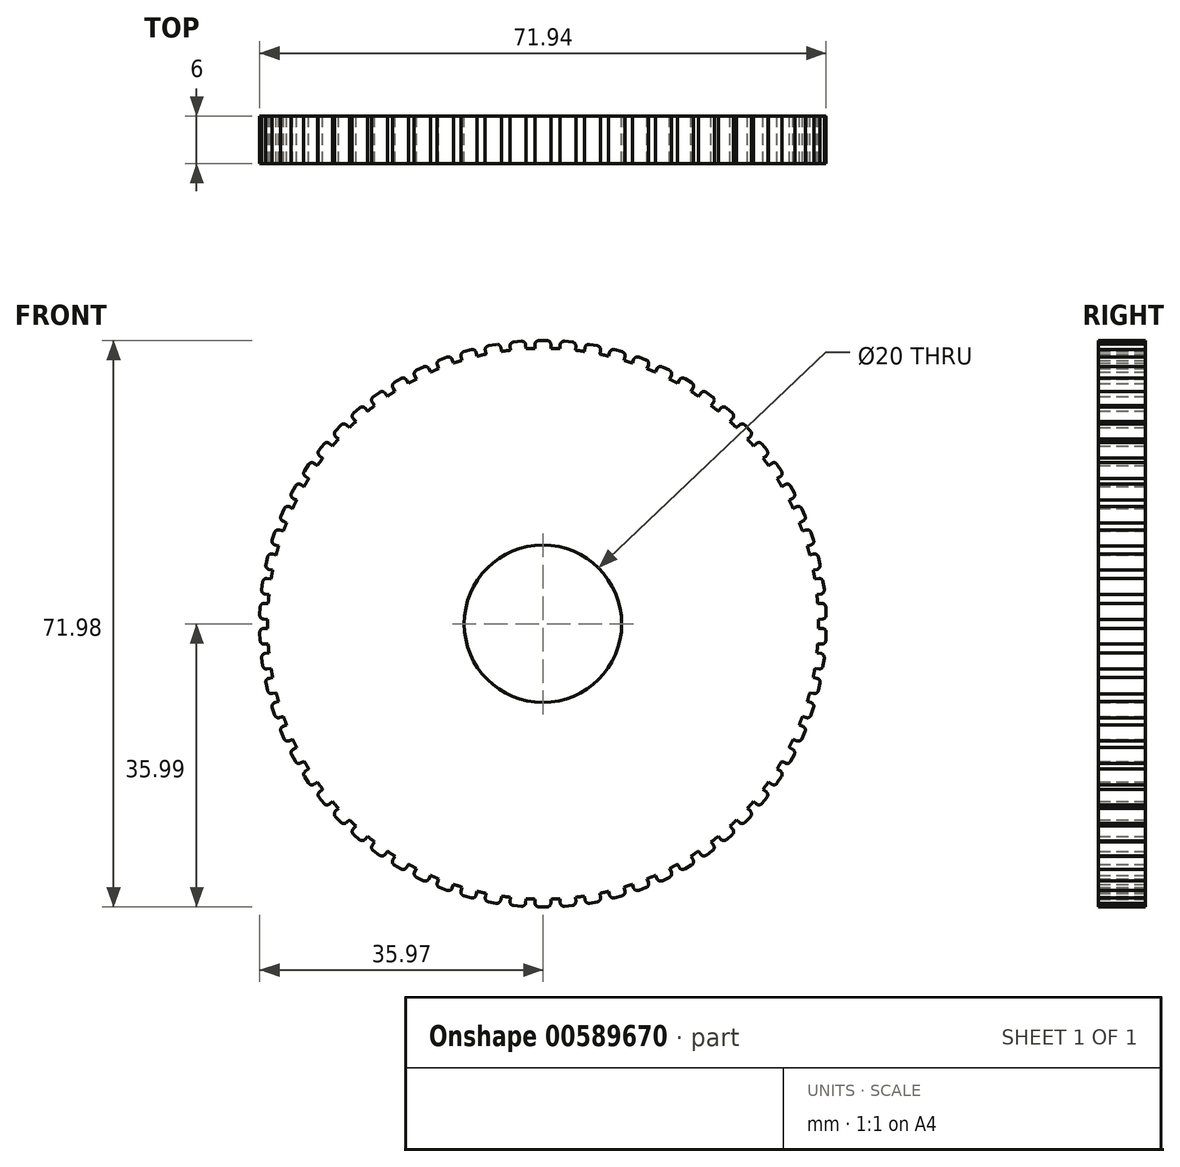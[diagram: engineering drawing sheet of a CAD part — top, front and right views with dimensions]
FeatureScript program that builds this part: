
annotation { "Feature Type Name" : "Feature", "Feature Type Description" : "" }
export const myFeature = defineFeature(function(context is Context, id is Id, definition is map)
    precondition{}
    {
        {
            var Q0;
            Q0=qCreatedBy(makeId("Front.planeOp"),FACE);
            var sketch = newSketch(context, id + "F0", { "sketchPlane" : qUnion([Q0])});
            skArc(sketch, "E0", {"start": v(-1, 34.99) * mm, "mid": v(-1.57, 34.96) * mm, "end": v(-2.14, 34.93) * mm});
            skLineSegment(sketch, "E1", {"start": v(-1, 34.99) * mm, "end": v(-1, 35.49) * mm});
            skLineSegment(sketch, "E2", {"start": v(-0.5, 35.99) * mm, "end": v(0.5, 35.99) * mm});
            skLineSegment(sketch, "E3", {"start": v(1, 35.49) * mm, "end": v(1, 34.99) * mm});
            skLineSegment(sketch, "E4", {"start": v(-2.15, 34.93) * mm, "end": v(-2.15, 35.96) * mm, "construction": true});
            skPoint(sketch, "E5.visualSharp", {"position": v(-1, 35.99) * mm});
            skArc(sketch, "E5.filletArc", {"start": v(-0.5, 35.99) * mm, "mid": v(-0.85, 35.84) * mm, "end": v(-1, 35.49) * mm});
            skPoint(sketch, "E6.visualSharp", {"position": v(1, 35.99) * mm});
            skArc(sketch, "E6.filletArc", {"start": v(1, 35.49) * mm, "mid": v(0.85, 35.84) * mm, "end": v(0.5, 35.99) * mm});
            skLineSegment(sketch, "E7.1.0", {"start": v(-4.13, 34.76) * mm, "end": v(-4.18, 35.25) * mm});
            skArc(sketch, "E7.1.1", {"start": v(-3.72, 35.8) * mm, "mid": v(-4.06, 35.62) * mm, "end": v(-4.18, 35.25) * mm});
            skLineSegment(sketch, "E7.1.2", {"start": v(-3.72, 35.8) * mm, "end": v(-2.73, 35.89) * mm});
            skArc(sketch, "E7.1.3", {"start": v(-2.18, 35.43) * mm, "mid": v(-2.36, 35.77) * mm, "end": v(-2.73, 35.89) * mm});
            skLineSegment(sketch, "E7.1.4", {"start": v(-2.18, 35.43) * mm, "end": v(-2.14, 34.93) * mm});
            skLineSegment(sketch, "E7.1.5", {"start": v(-5.27, 34.6) * mm, "end": v(-5.36, 35.62) * mm, "construction": true});
            skLineSegment(sketch, "E7.2.0", {"start": v(-7.23, 34.24) * mm, "end": v(-7.32, 34.74) * mm});
            skArc(sketch, "E7.2.1", {"start": v(-6.92, 35.32) * mm, "mid": v(-7.24, 35.11) * mm, "end": v(-7.32, 34.74) * mm});
            skLineSegment(sketch, "E7.2.2", {"start": v(-6.92, 35.32) * mm, "end": v(-5.93, 35.5) * mm});
            skArc(sketch, "E7.2.3", {"start": v(-5.35, 35.1) * mm, "mid": v(-5.56, 35.42) * mm, "end": v(-5.93, 35.5) * mm});
            skLineSegment(sketch, "E7.2.4", {"start": v(-5.35, 35.1) * mm, "end": v(-5.26, 34.6) * mm});
            skLineSegment(sketch, "E7.2.5", {"start": v(-8.35, 33.99) * mm, "end": v(-8.53, 35) * mm, "construction": true});
            skLineSegment(sketch, "E7.3.0", {"start": v(-10.27, 33.46) * mm, "end": v(-10.4, 33.94) * mm});
            skArc(sketch, "E7.3.1", {"start": v(-10.06, 34.56) * mm, "mid": v(-10.36, 34.32) * mm, "end": v(-10.4, 33.94) * mm});
            skLineSegment(sketch, "E7.3.2", {"start": v(-10.06, 34.56) * mm, "end": v(-9.1, 34.82) * mm});
            skArc(sketch, "E7.3.3", {"start": v(-8.48, 34.47) * mm, "mid": v(-8.71, 34.77) * mm, "end": v(-9.1, 34.82) * mm});
            skLineSegment(sketch, "E7.3.4", {"start": v(-8.48, 34.47) * mm, "end": v(-8.34, 34) * mm});
            skLineSegment(sketch, "E7.3.5", {"start": v(-11.36, 33.1) * mm, "end": v(-11.64, 34.1) * mm, "construction": true});
            skLineSegment(sketch, "E7.4.0", {"start": v(-13.23, 32.4) * mm, "end": v(-13.4, 32.87) * mm});
            skArc(sketch, "E7.4.1", {"start": v(-13.11, 33.52) * mm, "mid": v(-13.4, 33.25) * mm, "end": v(-13.4, 32.87) * mm});
            skLineSegment(sketch, "E7.4.2", {"start": v(-13.11, 33.52) * mm, "end": v(-12.18, 33.87) * mm});
            skArc(sketch, "E7.4.3", {"start": v(-11.53, 33.57) * mm, "mid": v(-11.8, 33.85) * mm, "end": v(-12.18, 33.87) * mm});
            skLineSegment(sketch, "E7.4.4", {"start": v(-11.53, 33.57) * mm, "end": v(-11.36, 33.1) * mm});
            skLineSegment(sketch, "E7.4.5", {"start": v(-14.28, 31.95) * mm, "end": v(-14.65, 32.91) * mm, "construction": true});
            skLineSegment(sketch, "E7.5.0", {"start": v(-16.08, 31.09) * mm, "end": v(-16.3, 31.54) * mm});
            skArc(sketch, "E7.5.1", {"start": v(-16.06, 32.2) * mm, "mid": v(-16.32, 31.92) * mm, "end": v(-16.3, 31.54) * mm});
            skLineSegment(sketch, "E7.5.2", {"start": v(-16.06, 32.2) * mm, "end": v(-15.16, 32.64) * mm});
            skArc(sketch, "E7.5.3", {"start": v(-14.5, 32.4) * mm, "mid": v(-14.78, 32.66) * mm, "end": v(-15.16, 32.64) * mm});
            skLineSegment(sketch, "E7.5.4", {"start": v(-14.5, 32.4) * mm, "end": v(-14.28, 31.95) * mm});
            skLineSegment(sketch, "E7.5.5", {"start": v(-17.1, 30.54) * mm, "end": v(-17.54, 31.47) * mm, "construction": true});
            skLineSegment(sketch, "E7.6.0", {"start": v(-18.8, 29.52) * mm, "end": v(-19.06, 29.95) * mm});
            skArc(sketch, "E7.6.1", {"start": v(-18.89, 30.64) * mm, "mid": v(-19.11, 30.33) * mm, "end": v(-19.06, 29.95) * mm});
            skLineSegment(sketch, "E7.6.2", {"start": v(-18.89, 30.64) * mm, "end": v(-18.03, 31.15) * mm});
            skArc(sketch, "E7.6.3", {"start": v(-17.34, 30.98) * mm, "mid": v(-17.65, 31.2) * mm, "end": v(-18.03, 31.15) * mm});
            skLineSegment(sketch, "E7.6.4", {"start": v(-17.34, 30.98) * mm, "end": v(-17.09, 30.55) * mm});
            skLineSegment(sketch, "E7.6.5", {"start": v(-19.76, 28.89) * mm, "end": v(-20.29, 29.77) * mm, "construction": true});
            skLineSegment(sketch, "E7.7.0", {"start": v(-21.37, 27.72) * mm, "end": v(-21.67, 28.12) * mm});
            skArc(sketch, "E7.7.1", {"start": v(-21.56, 28.82) * mm, "mid": v(-21.76, 28.5) * mm, "end": v(-21.67, 28.12) * mm});
            skLineSegment(sketch, "E7.7.2", {"start": v(-21.56, 28.82) * mm, "end": v(-20.75, 29.4) * mm});
            skArc(sketch, "E7.7.3", {"start": v(-20.05, 29.3) * mm, "mid": v(-20.38, 29.5) * mm, "end": v(-20.75, 29.4) * mm});
            skLineSegment(sketch, "E7.7.4", {"start": v(-20.05, 29.3) * mm, "end": v(-19.76, 28.9) * mm});
            skLineSegment(sketch, "E7.7.5", {"start": v(-22.27, 27) * mm, "end": v(-22.87, 27.83) * mm, "construction": true});
            skLineSegment(sketch, "E7.8.0", {"start": v(-23.77, 25.69) * mm, "end": v(-24.1, 26.07) * mm});
            skArc(sketch, "E7.8.1", {"start": v(-24.05, 26.77) * mm, "mid": v(-24.22, 26.43) * mm, "end": v(-24.1, 26.07) * mm});
            skLineSegment(sketch, "E7.8.2", {"start": v(-24.05, 26.77) * mm, "end": v(-23.3, 27.43) * mm});
            skArc(sketch, "E7.8.3", {"start": v(-22.6, 27.38) * mm, "mid": v(-22.94, 27.55) * mm, "end": v(-23.3, 27.43) * mm});
            skLineSegment(sketch, "E7.8.4", {"start": v(-22.6, 27.38) * mm, "end": v(-22.27, 27) * mm});
            skLineSegment(sketch, "E7.8.5", {"start": v(-24.6, 24.9) * mm, "end": v(-25.28, 25.67) * mm, "construction": true});
            skLineSegment(sketch, "E7.9.0", {"start": v(-25.98, 23.45) * mm, "end": v(-26.34, 23.8) * mm});
            skArc(sketch, "E7.9.1", {"start": v(-26.36, 24.5) * mm, "mid": v(-26.5, 24.15) * mm, "end": v(-26.34, 23.8) * mm});
            skLineSegment(sketch, "E7.9.2", {"start": v(-26.36, 24.5) * mm, "end": v(-25.66, 25.23) * mm});
            skArc(sketch, "E7.9.3", {"start": v(-24.96, 25.25) * mm, "mid": v(-25.31, 25.38) * mm, "end": v(-25.66, 25.23) * mm});
            skLineSegment(sketch, "E7.9.4", {"start": v(-24.96, 25.25) * mm, "end": v(-24.6, 24.9) * mm});
            skLineSegment(sketch, "E7.9.5", {"start": v(-26.73, 22.6) * mm, "end": v(-27.48, 23.3) * mm, "construction": true});
            skLineSegment(sketch, "E7.10.0", {"start": v(-27.98, 21.03) * mm, "end": v(-28.37, 21.34) * mm});
            skArc(sketch, "E7.10.1", {"start": v(-28.45, 22.05) * mm, "mid": v(-28.55, 21.68) * mm, "end": v(-28.37, 21.34) * mm});
            skLineSegment(sketch, "E7.10.2", {"start": v(-28.45, 22.05) * mm, "end": v(-27.82, 22.83) * mm});
            skArc(sketch, "E7.10.3", {"start": v(-27.12, 22.9) * mm, "mid": v(-27.49, 23.01) * mm, "end": v(-27.82, 22.83) * mm});
            skLineSegment(sketch, "E7.10.4", {"start": v(-27.12, 22.9) * mm, "end": v(-26.73, 22.6) * mm});
            skLineSegment(sketch, "E7.10.5", {"start": v(-28.65, 20.1) * mm, "end": v(-29.45, 20.74) * mm, "construction": true});
            skLineSegment(sketch, "E7.11.0", {"start": v(-29.75, 18.44) * mm, "end": v(-30.17, 18.71) * mm});
            skArc(sketch, "E7.11.1", {"start": v(-30.3, 19.4) * mm, "mid": v(-30.38, 19.03) * mm, "end": v(-30.17, 18.71) * mm});
            skLineSegment(sketch, "E7.11.2", {"start": v(-30.3, 19.4) * mm, "end": v(-29.76, 20.24) * mm});
            skArc(sketch, "E7.11.3", {"start": v(-29.06, 20.38) * mm, "mid": v(-29.44, 20.46) * mm, "end": v(-29.76, 20.24) * mm});
            skLineSegment(sketch, "E7.11.4", {"start": v(-29.06, 20.38) * mm, "end": v(-28.65, 20.1) * mm});
            skLineSegment(sketch, "E7.11.5", {"start": v(-30.34, 17.45) * mm, "end": v(-31.2, 18.02) * mm, "construction": true});
            skLineSegment(sketch, "E7.12.0", {"start": v(-31.28, 15.7) * mm, "end": v(-31.72, 15.93) * mm});
            skArc(sketch, "E7.12.1", {"start": v(-31.93, 16.61) * mm, "mid": v(-31.96, 16.23) * mm, "end": v(-31.72, 15.93) * mm});
            skLineSegment(sketch, "E7.12.2", {"start": v(-31.93, 16.61) * mm, "end": v(-31.45, 17.5) * mm});
            skArc(sketch, "E7.12.3", {"start": v(-30.77, 17.7) * mm, "mid": v(-31.16, 17.73) * mm, "end": v(-31.45, 17.5) * mm});
            skLineSegment(sketch, "E7.12.4", {"start": v(-30.77, 17.7) * mm, "end": v(-30.33, 17.46) * mm});
            skLineSegment(sketch, "E7.12.5", {"start": v(-31.78, 14.66) * mm, "end": v(-32.68, 15.15) * mm, "construction": true});
            skLineSegment(sketch, "E7.13.0", {"start": v(-32.56, 12.83) * mm, "end": v(-33.02, 13.03) * mm});
            skArc(sketch, "E7.13.1", {"start": v(-33.29, 13.68) * mm, "mid": v(-33.3, 13.3) * mm, "end": v(-33.02, 13.03) * mm});
            skLineSegment(sketch, "E7.13.2", {"start": v(-33.29, 13.68) * mm, "end": v(-32.9, 14.6) * mm});
            skArc(sketch, "E7.13.3", {"start": v(-32.24, 14.87) * mm, "mid": v(-32.62, 14.87) * mm, "end": v(-32.9, 14.6) * mm});
            skLineSegment(sketch, "E7.13.4", {"start": v(-32.24, 14.87) * mm, "end": v(-31.78, 14.67) * mm});
            skLineSegment(sketch, "E7.13.5", {"start": v(-32.97, 11.76) * mm, "end": v(-33.91, 12.16) * mm, "construction": true});
            skLineSegment(sketch, "E7.14.0", {"start": v(-33.58, 9.86) * mm, "end": v(-34.06, 10.01) * mm});
            skArc(sketch, "E7.14.1", {"start": v(-34.38, 10.64) * mm, "mid": v(-34.35, 10.26) * mm, "end": v(-34.06, 10.01) * mm});
            skLineSegment(sketch, "E7.14.2", {"start": v(-34.38, 10.64) * mm, "end": v(-34.07, 11.6) * mm});
            skArc(sketch, "E7.14.3", {"start": v(-33.44, 11.92) * mm, "mid": v(-33.82, 11.89) * mm, "end": v(-34.07, 11.6) * mm});
            skLineSegment(sketch, "E7.14.4", {"start": v(-33.44, 11.92) * mm, "end": v(-32.96, 11.76) * mm});
            skLineSegment(sketch, "E7.14.5", {"start": v(-33.89, 8.75) * mm, "end": v(-34.86, 9.07) * mm, "construction": true});
            skLineSegment(sketch, "E7.15.0", {"start": v(-34.33, 6.81) * mm, "end": v(-34.82, 6.92) * mm});
            skArc(sketch, "E7.15.1", {"start": v(-35.2, 7.52) * mm, "mid": v(-35.13, 7.14) * mm, "end": v(-34.82, 6.92) * mm});
            skLineSegment(sketch, "E7.15.2", {"start": v(-35.2, 7.52) * mm, "end": v(-34.97, 8.5) * mm});
            skArc(sketch, "E7.15.3", {"start": v(-34.37, 8.87) * mm, "mid": v(-34.75, 8.8) * mm, "end": v(-34.97, 8.5) * mm});
            skLineSegment(sketch, "E7.15.4", {"start": v(-34.37, 8.87) * mm, "end": v(-33.89, 8.76) * mm});
            skLineSegment(sketch, "E7.15.5", {"start": v(-34.54, 5.68) * mm, "end": v(-35.54, 5.91) * mm, "construction": true});
            skLineSegment(sketch, "E7.16.0", {"start": v(-34.8, 3.7) * mm, "end": v(-35.3, 3.77) * mm});
            skArc(sketch, "E7.16.1", {"start": v(-35.73, 4.34) * mm, "mid": v(-35.63, 3.96) * mm, "end": v(-35.3, 3.77) * mm});
            skLineSegment(sketch, "E7.16.2", {"start": v(-35.73, 4.34) * mm, "end": v(-35.6, 5.33) * mm});
            skArc(sketch, "E7.16.3", {"start": v(-35.03, 5.75) * mm, "mid": v(-35.4, 5.66) * mm, "end": v(-35.6, 5.33) * mm});
            skLineSegment(sketch, "E7.16.4", {"start": v(-35.03, 5.75) * mm, "end": v(-34.53, 5.69) * mm});
            skLineSegment(sketch, "E7.16.5", {"start": v(-34.9, 2.56) * mm, "end": v(-35.92, 2.7) * mm, "construction": true});
            skLineSegment(sketch, "E7.17.0", {"start": v(-35, 0.57) * mm, "end": v(-35.5, 0.6) * mm});
            skArc(sketch, "E7.17.1", {"start": v(-35.97, 1.11) * mm, "mid": v(-35.84, 0.76) * mm, "end": v(-35.5, 0.6) * mm});
            skLineSegment(sketch, "E7.17.2", {"start": v(-35.97, 1.11) * mm, "end": v(-35.93, 2.11) * mm});
            skArc(sketch, "E7.17.3", {"start": v(-35.4, 2.6) * mm, "mid": v(-35.76, 2.46) * mm, "end": v(-35.93, 2.11) * mm});
            skLineSegment(sketch, "E7.17.4", {"start": v(-35.4, 2.6) * mm, "end": v(-34.9, 2.57) * mm});
            skLineSegment(sketch, "E7.17.5", {"start": v(-35, -0.58) * mm, "end": v(-36.02, -0.53) * mm, "construction": true});
            skLineSegment(sketch, "E7.18.0", {"start": v(-34.9, -2.57) * mm, "end": v(-35.4, -2.6) * mm});
            skArc(sketch, "E7.18.1", {"start": v(-35.93, -2.11) * mm, "mid": v(-35.76, -2.46) * mm, "end": v(-35.4, -2.6) * mm});
            skLineSegment(sketch, "E7.18.2", {"start": v(-35.93, -2.11) * mm, "end": v(-35.97, -1.11) * mm});
            skArc(sketch, "E7.18.3", {"start": v(-35.5, -0.6) * mm, "mid": v(-35.84, -0.76) * mm, "end": v(-35.97, -1.11) * mm});
            skLineSegment(sketch, "E7.18.4", {"start": v(-35.5, -0.6) * mm, "end": v(-35, -0.57) * mm});
            skLineSegment(sketch, "E7.18.5", {"start": v(-34.8, -3.71) * mm, "end": v(-35.83, -3.76) * mm, "construction": true});
            skLineSegment(sketch, "E7.19.0", {"start": v(-34.53, -5.69) * mm, "end": v(-35.03, -5.75) * mm});
            skArc(sketch, "E7.19.1", {"start": v(-35.6, -5.33) * mm, "mid": v(-35.4, -5.66) * mm, "end": v(-35.03, -5.75) * mm});
            skLineSegment(sketch, "E7.19.2", {"start": v(-35.6, -5.33) * mm, "end": v(-35.73, -4.34) * mm});
            skArc(sketch, "E7.19.3", {"start": v(-35.3, -3.77) * mm, "mid": v(-35.63, -3.96) * mm, "end": v(-35.73, -4.34) * mm});
            skLineSegment(sketch, "E7.19.4", {"start": v(-35.3, -3.77) * mm, "end": v(-34.8, -3.7) * mm});
            skLineSegment(sketch, "E7.19.5", {"start": v(-34.33, -6.82) * mm, "end": v(-35.35, -6.95) * mm, "construction": true});
            skLineSegment(sketch, "E7.20.0", {"start": v(-33.89, -8.76) * mm, "end": v(-34.37, -8.87) * mm});
            skArc(sketch, "E7.20.1", {"start": v(-34.97, -8.5) * mm, "mid": v(-34.75, -8.8) * mm, "end": v(-34.37, -8.87) * mm});
            skLineSegment(sketch, "E7.20.2", {"start": v(-34.97, -8.5) * mm, "end": v(-35.2, -7.52) * mm});
            skArc(sketch, "E7.20.3", {"start": v(-34.82, -6.92) * mm, "mid": v(-35.13, -7.14) * mm, "end": v(-35.2, -7.52) * mm});
            skLineSegment(sketch, "E7.20.4", {"start": v(-34.82, -6.92) * mm, "end": v(-34.33, -6.81) * mm});
            skLineSegment(sketch, "E7.20.5", {"start": v(-33.58, -9.87) * mm, "end": v(-34.58, -10.1) * mm, "construction": true});
            skLineSegment(sketch, "E7.21.0", {"start": v(-32.96, -11.76) * mm, "end": v(-33.44, -11.92) * mm});
            skArc(sketch, "E7.21.1", {"start": v(-34.07, -11.6) * mm, "mid": v(-33.82, -11.89) * mm, "end": v(-33.44, -11.92) * mm});
            skLineSegment(sketch, "E7.21.2", {"start": v(-34.07, -11.6) * mm, "end": v(-34.38, -10.64) * mm});
            skArc(sketch, "E7.21.3", {"start": v(-34.06, -10.01) * mm, "mid": v(-34.35, -10.26) * mm, "end": v(-34.38, -10.64) * mm});
            skLineSegment(sketch, "E7.21.4", {"start": v(-34.06, -10.01) * mm, "end": v(-33.58, -9.86) * mm});
            skLineSegment(sketch, "E7.21.5", {"start": v(-32.56, -12.84) * mm, "end": v(-33.54, -13.15) * mm, "construction": true});
            skLineSegment(sketch, "E7.22.0", {"start": v(-31.78, -14.67) * mm, "end": v(-32.24, -14.87) * mm});
            skArc(sketch, "E7.22.1", {"start": v(-32.9, -14.6) * mm, "mid": v(-32.62, -14.87) * mm, "end": v(-32.24, -14.87) * mm});
            skLineSegment(sketch, "E7.22.2", {"start": v(-32.9, -14.6) * mm, "end": v(-33.29, -13.68) * mm});
            skArc(sketch, "E7.22.3", {"start": v(-33.02, -13.03) * mm, "mid": v(-33.3, -13.3) * mm, "end": v(-33.29, -13.68) * mm});
            skLineSegment(sketch, "E7.22.4", {"start": v(-33.02, -13.03) * mm, "end": v(-32.56, -12.83) * mm});
            skLineSegment(sketch, "E7.22.5", {"start": v(-31.28, -15.7) * mm, "end": v(-32.22, -16.1) * mm, "construction": true});
            skLineSegment(sketch, "E7.23.0", {"start": v(-30.33, -17.46) * mm, "end": v(-30.77, -17.7) * mm});
            skArc(sketch, "E7.23.1", {"start": v(-31.45, -17.5) * mm, "mid": v(-31.16, -17.73) * mm, "end": v(-30.77, -17.7) * mm});
            skLineSegment(sketch, "E7.23.2", {"start": v(-31.45, -17.5) * mm, "end": v(-31.93, -16.61) * mm});
            skArc(sketch, "E7.23.3", {"start": v(-31.72, -15.93) * mm, "mid": v(-31.96, -16.23) * mm, "end": v(-31.93, -16.61) * mm});
            skLineSegment(sketch, "E7.23.4", {"start": v(-31.72, -15.93) * mm, "end": v(-31.28, -15.7) * mm});
            skLineSegment(sketch, "E7.23.5", {"start": v(-29.75, -18.44) * mm, "end": v(-30.65, -18.93) * mm, "construction": true});
            skLineSegment(sketch, "E7.24.0", {"start": v(-28.65, -20.1) * mm, "end": v(-29.06, -20.38) * mm});
            skArc(sketch, "E7.24.1", {"start": v(-29.76, -20.24) * mm, "mid": v(-29.44, -20.46) * mm, "end": v(-29.06, -20.38) * mm});
            skLineSegment(sketch, "E7.24.2", {"start": v(-29.76, -20.24) * mm, "end": v(-30.3, -19.4) * mm});
            skArc(sketch, "E7.24.3", {"start": v(-30.17, -18.71) * mm, "mid": v(-30.38, -19.03) * mm, "end": v(-30.3, -19.4) * mm});
            skLineSegment(sketch, "E7.24.4", {"start": v(-30.17, -18.71) * mm, "end": v(-29.75, -18.44) * mm});
            skLineSegment(sketch, "E7.24.5", {"start": v(-27.97, -21.04) * mm, "end": v(-28.83, -21.6) * mm, "construction": true});
            skLineSegment(sketch, "E7.25.0", {"start": v(-26.73, -22.6) * mm, "end": v(-27.12, -22.9) * mm});
            skArc(sketch, "E7.25.1", {"start": v(-27.82, -22.83) * mm, "mid": v(-27.49, -23.01) * mm, "end": v(-27.12, -22.9) * mm});
            skLineSegment(sketch, "E7.25.2", {"start": v(-27.82, -22.83) * mm, "end": v(-28.45, -22.05) * mm});
            skArc(sketch, "E7.25.3", {"start": v(-28.37, -21.34) * mm, "mid": v(-28.55, -21.68) * mm, "end": v(-28.45, -22.05) * mm});
            skLineSegment(sketch, "E7.25.4", {"start": v(-28.37, -21.34) * mm, "end": v(-27.98, -21.03) * mm});
            skLineSegment(sketch, "E7.25.5", {"start": v(-25.97, -23.46) * mm, "end": v(-26.78, -24.1) * mm, "construction": true});
            skLineSegment(sketch, "E7.26.0", {"start": v(-24.6, -24.9) * mm, "end": v(-24.96, -25.25) * mm});
            skArc(sketch, "E7.26.1", {"start": v(-25.66, -25.23) * mm, "mid": v(-25.31, -25.38) * mm, "end": v(-24.96, -25.25) * mm});
            skLineSegment(sketch, "E7.26.2", {"start": v(-25.66, -25.23) * mm, "end": v(-26.36, -24.5) * mm});
            skArc(sketch, "E7.26.3", {"start": v(-26.34, -23.8) * mm, "mid": v(-26.5, -24.15) * mm, "end": v(-26.36, -24.5) * mm});
            skLineSegment(sketch, "E7.26.4", {"start": v(-26.34, -23.8) * mm, "end": v(-25.98, -23.45) * mm});
            skLineSegment(sketch, "E7.26.5", {"start": v(-23.77, -25.7) * mm, "end": v(-24.5, -26.4) * mm, "construction": true});
            skLineSegment(sketch, "E7.27.0", {"start": v(-22.27, -27) * mm, "end": v(-22.6, -27.38) * mm});
            skArc(sketch, "E7.27.1", {"start": v(-23.3, -27.43) * mm, "mid": v(-22.94, -27.55) * mm, "end": v(-22.6, -27.38) * mm});
            skLineSegment(sketch, "E7.27.2", {"start": v(-23.3, -27.43) * mm, "end": v(-24.05, -26.77) * mm});
            skArc(sketch, "E7.27.3", {"start": v(-24.1, -26.07) * mm, "mid": v(-24.22, -26.43) * mm, "end": v(-24.05, -26.77) * mm});
            skLineSegment(sketch, "E7.27.4", {"start": v(-24.1, -26.07) * mm, "end": v(-23.77, -25.69) * mm});
            skLineSegment(sketch, "E7.27.5", {"start": v(-21.37, -27.72) * mm, "end": v(-22.04, -28.5) * mm, "construction": true});
            skLineSegment(sketch, "E7.28.0", {"start": v(-19.76, -28.9) * mm, "end": v(-20.05, -29.3) * mm});
            skArc(sketch, "E7.28.1", {"start": v(-20.75, -29.4) * mm, "mid": v(-20.38, -29.5) * mm, "end": v(-20.05, -29.3) * mm});
            skLineSegment(sketch, "E7.28.2", {"start": v(-20.75, -29.4) * mm, "end": v(-21.56, -28.82) * mm});
            skArc(sketch, "E7.28.3", {"start": v(-21.67, -28.12) * mm, "mid": v(-21.76, -28.5) * mm, "end": v(-21.56, -28.82) * mm});
            skLineSegment(sketch, "E7.28.4", {"start": v(-21.67, -28.12) * mm, "end": v(-21.37, -27.72) * mm});
            skLineSegment(sketch, "E7.28.5", {"start": v(-18.8, -29.52) * mm, "end": v(-19.4, -30.36) * mm, "construction": true});
            skLineSegment(sketch, "E7.29.0", {"start": v(-17.09, -30.55) * mm, "end": v(-17.34, -30.98) * mm});
            skArc(sketch, "E7.29.1", {"start": v(-18.03, -31.15) * mm, "mid": v(-17.65, -31.2) * mm, "end": v(-17.34, -30.98) * mm});
            skLineSegment(sketch, "E7.29.2", {"start": v(-18.03, -31.15) * mm, "end": v(-18.89, -30.64) * mm});
            skArc(sketch, "E7.29.3", {"start": v(-19.06, -29.95) * mm, "mid": v(-19.11, -30.33) * mm, "end": v(-18.89, -30.64) * mm});
            skLineSegment(sketch, "E7.29.4", {"start": v(-19.06, -29.95) * mm, "end": v(-18.8, -29.52) * mm});
            skLineSegment(sketch, "E7.29.5", {"start": v(-16.08, -31.09) * mm, "end": v(-16.6, -31.97) * mm, "construction": true});
            skLineSegment(sketch, "E7.30.0", {"start": v(-14.28, -31.95) * mm, "end": v(-14.5, -32.4) * mm});
            skArc(sketch, "E7.30.1", {"start": v(-15.16, -32.64) * mm, "mid": v(-14.78, -32.66) * mm, "end": v(-14.5, -32.4) * mm});
            skLineSegment(sketch, "E7.30.2", {"start": v(-15.16, -32.64) * mm, "end": v(-16.06, -32.2) * mm});
            skArc(sketch, "E7.30.3", {"start": v(-16.3, -31.54) * mm, "mid": v(-16.32, -31.92) * mm, "end": v(-16.06, -32.2) * mm});
            skLineSegment(sketch, "E7.30.4", {"start": v(-16.3, -31.54) * mm, "end": v(-16.08, -31.09) * mm});
            skLineSegment(sketch, "E7.30.5", {"start": v(-13.22, -32.4) * mm, "end": v(-13.67, -33.33) * mm, "construction": true});
            skLineSegment(sketch, "E7.31.0", {"start": v(-11.36, -33.1) * mm, "end": v(-11.53, -33.57) * mm});
            skArc(sketch, "E7.31.1", {"start": v(-12.18, -33.87) * mm, "mid": v(-11.8, -33.85) * mm, "end": v(-11.53, -33.57) * mm});
            skLineSegment(sketch, "E7.31.2", {"start": v(-12.18, -33.87) * mm, "end": v(-13.11, -33.52) * mm});
            skArc(sketch, "E7.31.3", {"start": v(-13.4, -32.87) * mm, "mid": v(-13.4, -33.25) * mm, "end": v(-13.11, -33.52) * mm});
            skLineSegment(sketch, "E7.31.4", {"start": v(-13.4, -32.87) * mm, "end": v(-13.23, -32.4) * mm});
            skLineSegment(sketch, "E7.31.5", {"start": v(-10.27, -33.46) * mm, "end": v(-10.63, -34.42) * mm, "construction": true});
            skLineSegment(sketch, "E7.32.0", {"start": v(-8.34, -34) * mm, "end": v(-8.48, -34.47) * mm});
            skArc(sketch, "E7.32.1", {"start": v(-9.1, -34.82) * mm, "mid": v(-8.71, -34.77) * mm, "end": v(-8.48, -34.47) * mm});
            skLineSegment(sketch, "E7.32.2", {"start": v(-9.1, -34.82) * mm, "end": v(-10.06, -34.56) * mm});
            skArc(sketch, "E7.32.3", {"start": v(-10.4, -33.94) * mm, "mid": v(-10.36, -34.32) * mm, "end": v(-10.06, -34.56) * mm});
            skLineSegment(sketch, "E7.32.4", {"start": v(-10.4, -33.94) * mm, "end": v(-10.27, -33.46) * mm});
            skLineSegment(sketch, "E7.32.5", {"start": v(-7.23, -34.25) * mm, "end": v(-7.5, -35.24) * mm, "construction": true});
            skLineSegment(sketch, "E7.33.0", {"start": v(-5.26, -34.6) * mm, "end": v(-5.35, -35.1) * mm});
            skArc(sketch, "E7.33.1", {"start": v(-5.93, -35.5) * mm, "mid": v(-5.56, -35.42) * mm, "end": v(-5.35, -35.1) * mm});
            skLineSegment(sketch, "E7.33.2", {"start": v(-5.93, -35.5) * mm, "end": v(-6.92, -35.32) * mm});
            skArc(sketch, "E7.33.3", {"start": v(-7.32, -34.74) * mm, "mid": v(-7.24, -35.11) * mm, "end": v(-6.92, -35.32) * mm});
            skLineSegment(sketch, "E7.33.4", {"start": v(-7.32, -34.74) * mm, "end": v(-7.23, -34.24) * mm});
            skLineSegment(sketch, "E7.33.5", {"start": v(-4.13, -34.76) * mm, "end": v(-4.3, -35.77) * mm, "construction": true});
            skLineSegment(sketch, "E7.34.0", {"start": v(-2.14, -34.93) * mm, "end": v(-2.18, -35.43) * mm});
            skArc(sketch, "E7.34.1", {"start": v(-2.73, -35.89) * mm, "mid": v(-2.36, -35.77) * mm, "end": v(-2.18, -35.43) * mm});
            skLineSegment(sketch, "E7.34.2", {"start": v(-2.73, -35.89) * mm, "end": v(-3.72, -35.8) * mm});
            skArc(sketch, "E7.34.3", {"start": v(-4.18, -35.25) * mm, "mid": v(-4.06, -35.62) * mm, "end": v(-3.72, -35.8) * mm});
            skLineSegment(sketch, "E7.34.4", {"start": v(-4.18, -35.25) * mm, "end": v(-4.13, -34.76) * mm});
            skLineSegment(sketch, "E7.34.5", {"start": v(-1, -34.99) * mm, "end": v(-1.09, -36) * mm, "construction": true});
            skLineSegment(sketch, "E7.35.0", {"start": v(1, -34.99) * mm, "end": v(1, -35.49) * mm});
            skArc(sketch, "E7.35.1", {"start": v(0.5, -35.99) * mm, "mid": v(0.85, -35.84) * mm, "end": v(1, -35.49) * mm});
            skLineSegment(sketch, "E7.35.2", {"start": v(0.5, -35.99) * mm, "end": v(-0.5, -35.99) * mm});
            skArc(sketch, "E7.35.3", {"start": v(-1, -35.49) * mm, "mid": v(-0.85, -35.84) * mm, "end": v(-0.5, -35.99) * mm});
            skLineSegment(sketch, "E7.35.4", {"start": v(-1, -35.49) * mm, "end": v(-1, -34.99) * mm});
            skLineSegment(sketch, "E7.35.5", {"start": v(2.15, -34.93) * mm, "end": v(2.15, -35.96) * mm, "construction": true});
            skLineSegment(sketch, "E7.36.0", {"start": v(4.13, -34.76) * mm, "end": v(4.18, -35.25) * mm});
            skArc(sketch, "E7.36.1", {"start": v(3.72, -35.8) * mm, "mid": v(4.06, -35.62) * mm, "end": v(4.18, -35.25) * mm});
            skLineSegment(sketch, "E7.36.2", {"start": v(3.72, -35.8) * mm, "end": v(2.73, -35.89) * mm});
            skArc(sketch, "E7.36.3", {"start": v(2.18, -35.43) * mm, "mid": v(2.36, -35.77) * mm, "end": v(2.73, -35.89) * mm});
            skLineSegment(sketch, "E7.36.4", {"start": v(2.18, -35.43) * mm, "end": v(2.14, -34.93) * mm});
            skLineSegment(sketch, "E7.36.5", {"start": v(5.27, -34.6) * mm, "end": v(5.36, -35.62) * mm, "construction": true});
            skLineSegment(sketch, "E7.37.0", {"start": v(7.23, -34.24) * mm, "end": v(7.32, -34.74) * mm});
            skArc(sketch, "E7.37.1", {"start": v(6.92, -35.32) * mm, "mid": v(7.24, -35.11) * mm, "end": v(7.32, -34.74) * mm});
            skLineSegment(sketch, "E7.37.2", {"start": v(6.92, -35.32) * mm, "end": v(5.93, -35.5) * mm});
            skArc(sketch, "E7.37.3", {"start": v(5.35, -35.1) * mm, "mid": v(5.56, -35.42) * mm, "end": v(5.93, -35.5) * mm});
            skLineSegment(sketch, "E7.37.4", {"start": v(5.35, -35.1) * mm, "end": v(5.26, -34.6) * mm});
            skLineSegment(sketch, "E7.37.5", {"start": v(8.35, -33.99) * mm, "end": v(8.53, -35) * mm, "construction": true});
            skLineSegment(sketch, "E7.38.0", {"start": v(10.27, -33.46) * mm, "end": v(10.4, -33.94) * mm});
            skArc(sketch, "E7.38.1", {"start": v(10.06, -34.56) * mm, "mid": v(10.36, -34.32) * mm, "end": v(10.4, -33.94) * mm});
            skLineSegment(sketch, "E7.38.2", {"start": v(10.06, -34.56) * mm, "end": v(9.1, -34.82) * mm});
            skArc(sketch, "E7.38.3", {"start": v(8.48, -34.47) * mm, "mid": v(8.71, -34.77) * mm, "end": v(9.1, -34.82) * mm});
            skLineSegment(sketch, "E7.38.4", {"start": v(8.48, -34.47) * mm, "end": v(8.34, -34) * mm});
            skLineSegment(sketch, "E7.38.5", {"start": v(11.36, -33.1) * mm, "end": v(11.64, -34.1) * mm, "construction": true});
            skLineSegment(sketch, "E7.39.0", {"start": v(13.23, -32.4) * mm, "end": v(13.4, -32.87) * mm});
            skArc(sketch, "E7.39.1", {"start": v(13.11, -33.52) * mm, "mid": v(13.4, -33.25) * mm, "end": v(13.4, -32.87) * mm});
            skLineSegment(sketch, "E7.39.2", {"start": v(13.11, -33.52) * mm, "end": v(12.18, -33.87) * mm});
            skArc(sketch, "E7.39.3", {"start": v(11.53, -33.57) * mm, "mid": v(11.8, -33.85) * mm, "end": v(12.18, -33.87) * mm});
            skLineSegment(sketch, "E7.39.4", {"start": v(11.53, -33.57) * mm, "end": v(11.36, -33.1) * mm});
            skLineSegment(sketch, "E7.39.5", {"start": v(14.28, -31.95) * mm, "end": v(14.65, -32.91) * mm, "construction": true});
            skLineSegment(sketch, "E7.40.0", {"start": v(16.08, -31.09) * mm, "end": v(16.3, -31.54) * mm});
            skArc(sketch, "E7.40.1", {"start": v(16.06, -32.2) * mm, "mid": v(16.32, -31.92) * mm, "end": v(16.3, -31.54) * mm});
            skLineSegment(sketch, "E7.40.2", {"start": v(16.06, -32.2) * mm, "end": v(15.16, -32.64) * mm});
            skArc(sketch, "E7.40.3", {"start": v(14.5, -32.4) * mm, "mid": v(14.78, -32.66) * mm, "end": v(15.16, -32.64) * mm});
            skLineSegment(sketch, "E7.40.4", {"start": v(14.5, -32.4) * mm, "end": v(14.28, -31.95) * mm});
            skLineSegment(sketch, "E7.40.5", {"start": v(17.1, -30.54) * mm, "end": v(17.54, -31.47) * mm, "construction": true});
            skLineSegment(sketch, "E7.41.0", {"start": v(18.8, -29.52) * mm, "end": v(19.06, -29.95) * mm});
            skArc(sketch, "E7.41.1", {"start": v(18.89, -30.64) * mm, "mid": v(19.11, -30.33) * mm, "end": v(19.06, -29.95) * mm});
            skLineSegment(sketch, "E7.41.2", {"start": v(18.89, -30.64) * mm, "end": v(18.03, -31.15) * mm});
            skArc(sketch, "E7.41.3", {"start": v(17.34, -30.98) * mm, "mid": v(17.65, -31.2) * mm, "end": v(18.03, -31.15) * mm});
            skLineSegment(sketch, "E7.41.4", {"start": v(17.34, -30.98) * mm, "end": v(17.09, -30.55) * mm});
            skLineSegment(sketch, "E7.41.5", {"start": v(19.76, -28.89) * mm, "end": v(20.29, -29.77) * mm, "construction": true});
            skLineSegment(sketch, "E7.42.0", {"start": v(21.37, -27.72) * mm, "end": v(21.67, -28.12) * mm});
            skArc(sketch, "E7.42.1", {"start": v(21.56, -28.82) * mm, "mid": v(21.76, -28.5) * mm, "end": v(21.67, -28.12) * mm});
            skLineSegment(sketch, "E7.42.2", {"start": v(21.56, -28.82) * mm, "end": v(20.75, -29.4) * mm});
            skArc(sketch, "E7.42.3", {"start": v(20.05, -29.3) * mm, "mid": v(20.38, -29.5) * mm, "end": v(20.75, -29.4) * mm});
            skLineSegment(sketch, "E7.42.4", {"start": v(20.05, -29.3) * mm, "end": v(19.76, -28.9) * mm});
            skLineSegment(sketch, "E7.42.5", {"start": v(22.27, -27) * mm, "end": v(22.87, -27.83) * mm, "construction": true});
            skLineSegment(sketch, "E7.43.0", {"start": v(23.77, -25.69) * mm, "end": v(24.1, -26.07) * mm});
            skArc(sketch, "E7.43.1", {"start": v(24.05, -26.77) * mm, "mid": v(24.22, -26.43) * mm, "end": v(24.1, -26.07) * mm});
            skLineSegment(sketch, "E7.43.2", {"start": v(24.05, -26.77) * mm, "end": v(23.3, -27.43) * mm});
            skArc(sketch, "E7.43.3", {"start": v(22.6, -27.38) * mm, "mid": v(22.94, -27.55) * mm, "end": v(23.3, -27.43) * mm});
            skLineSegment(sketch, "E7.43.4", {"start": v(22.6, -27.38) * mm, "end": v(22.27, -27) * mm});
            skLineSegment(sketch, "E7.43.5", {"start": v(24.6, -24.9) * mm, "end": v(25.28, -25.67) * mm, "construction": true});
            skLineSegment(sketch, "E7.44.0", {"start": v(25.98, -23.45) * mm, "end": v(26.34, -23.8) * mm});
            skArc(sketch, "E7.44.1", {"start": v(26.36, -24.5) * mm, "mid": v(26.5, -24.15) * mm, "end": v(26.34, -23.8) * mm});
            skLineSegment(sketch, "E7.44.2", {"start": v(26.36, -24.5) * mm, "end": v(25.66, -25.23) * mm});
            skArc(sketch, "E7.44.3", {"start": v(24.96, -25.25) * mm, "mid": v(25.31, -25.38) * mm, "end": v(25.66, -25.23) * mm});
            skLineSegment(sketch, "E7.44.4", {"start": v(24.96, -25.25) * mm, "end": v(24.6, -24.9) * mm});
            skLineSegment(sketch, "E7.44.5", {"start": v(26.73, -22.6) * mm, "end": v(27.48, -23.3) * mm, "construction": true});
            skLineSegment(sketch, "E7.45.0", {"start": v(27.98, -21.03) * mm, "end": v(28.37, -21.34) * mm});
            skArc(sketch, "E7.45.1", {"start": v(28.45, -22.05) * mm, "mid": v(28.55, -21.68) * mm, "end": v(28.37, -21.34) * mm});
            skLineSegment(sketch, "E7.45.2", {"start": v(28.45, -22.05) * mm, "end": v(27.82, -22.83) * mm});
            skArc(sketch, "E7.45.3", {"start": v(27.12, -22.9) * mm, "mid": v(27.49, -23.01) * mm, "end": v(27.82, -22.83) * mm});
            skLineSegment(sketch, "E7.45.4", {"start": v(27.12, -22.9) * mm, "end": v(26.73, -22.6) * mm});
            skLineSegment(sketch, "E7.45.5", {"start": v(28.65, -20.1) * mm, "end": v(29.45, -20.74) * mm, "construction": true});
            skLineSegment(sketch, "E7.46.0", {"start": v(29.75, -18.44) * mm, "end": v(30.17, -18.71) * mm});
            skArc(sketch, "E7.46.1", {"start": v(30.3, -19.4) * mm, "mid": v(30.38, -19.03) * mm, "end": v(30.17, -18.71) * mm});
            skLineSegment(sketch, "E7.46.2", {"start": v(30.3, -19.4) * mm, "end": v(29.76, -20.24) * mm});
            skArc(sketch, "E7.46.3", {"start": v(29.06, -20.38) * mm, "mid": v(29.44, -20.46) * mm, "end": v(29.76, -20.24) * mm});
            skLineSegment(sketch, "E7.46.4", {"start": v(29.06, -20.38) * mm, "end": v(28.65, -20.1) * mm});
            skLineSegment(sketch, "E7.46.5", {"start": v(30.34, -17.45) * mm, "end": v(31.2, -18.02) * mm, "construction": true});
            skLineSegment(sketch, "E7.47.0", {"start": v(31.28, -15.7) * mm, "end": v(31.72, -15.93) * mm});
            skArc(sketch, "E7.47.1", {"start": v(31.93, -16.61) * mm, "mid": v(31.96, -16.23) * mm, "end": v(31.72, -15.93) * mm});
            skLineSegment(sketch, "E7.47.2", {"start": v(31.93, -16.61) * mm, "end": v(31.45, -17.5) * mm});
            skArc(sketch, "E7.47.3", {"start": v(30.77, -17.7) * mm, "mid": v(31.16, -17.73) * mm, "end": v(31.45, -17.5) * mm});
            skLineSegment(sketch, "E7.47.4", {"start": v(30.77, -17.7) * mm, "end": v(30.33, -17.46) * mm});
            skLineSegment(sketch, "E7.47.5", {"start": v(31.78, -14.66) * mm, "end": v(32.68, -15.15) * mm, "construction": true});
            skLineSegment(sketch, "E7.48.0", {"start": v(32.56, -12.83) * mm, "end": v(33.02, -13.03) * mm});
            skArc(sketch, "E7.48.1", {"start": v(33.29, -13.68) * mm, "mid": v(33.3, -13.3) * mm, "end": v(33.02, -13.03) * mm});
            skLineSegment(sketch, "E7.48.2", {"start": v(33.29, -13.68) * mm, "end": v(32.9, -14.6) * mm});
            skArc(sketch, "E7.48.3", {"start": v(32.24, -14.87) * mm, "mid": v(32.62, -14.87) * mm, "end": v(32.9, -14.6) * mm});
            skLineSegment(sketch, "E7.48.4", {"start": v(32.24, -14.87) * mm, "end": v(31.78, -14.67) * mm});
            skLineSegment(sketch, "E7.48.5", {"start": v(32.97, -11.76) * mm, "end": v(33.91, -12.16) * mm, "construction": true});
            skLineSegment(sketch, "E7.49.0", {"start": v(33.58, -9.86) * mm, "end": v(34.06, -10.01) * mm});
            skArc(sketch, "E7.49.1", {"start": v(34.38, -10.64) * mm, "mid": v(34.35, -10.26) * mm, "end": v(34.06, -10.01) * mm});
            skLineSegment(sketch, "E7.49.2", {"start": v(34.38, -10.64) * mm, "end": v(34.07, -11.6) * mm});
            skArc(sketch, "E7.49.3", {"start": v(33.44, -11.92) * mm, "mid": v(33.82, -11.89) * mm, "end": v(34.07, -11.6) * mm});
            skLineSegment(sketch, "E7.49.4", {"start": v(33.44, -11.92) * mm, "end": v(32.96, -11.76) * mm});
            skLineSegment(sketch, "E7.49.5", {"start": v(33.89, -8.75) * mm, "end": v(34.86, -9.07) * mm, "construction": true});
            skLineSegment(sketch, "E7.50.0", {"start": v(34.33, -6.81) * mm, "end": v(34.82, -6.92) * mm});
            skArc(sketch, "E7.50.1", {"start": v(35.2, -7.52) * mm, "mid": v(35.13, -7.14) * mm, "end": v(34.82, -6.92) * mm});
            skLineSegment(sketch, "E7.50.2", {"start": v(35.2, -7.52) * mm, "end": v(34.97, -8.5) * mm});
            skArc(sketch, "E7.50.3", {"start": v(34.37, -8.87) * mm, "mid": v(34.75, -8.8) * mm, "end": v(34.97, -8.5) * mm});
            skLineSegment(sketch, "E7.50.4", {"start": v(34.37, -8.87) * mm, "end": v(33.89, -8.76) * mm});
            skLineSegment(sketch, "E7.50.5", {"start": v(34.54, -5.68) * mm, "end": v(35.54, -5.91) * mm, "construction": true});
            skLineSegment(sketch, "E7.51.0", {"start": v(34.8, -3.7) * mm, "end": v(35.3, -3.77) * mm});
            skArc(sketch, "E7.51.1", {"start": v(35.73, -4.34) * mm, "mid": v(35.63, -3.96) * mm, "end": v(35.3, -3.77) * mm});
            skLineSegment(sketch, "E7.51.2", {"start": v(35.73, -4.34) * mm, "end": v(35.6, -5.33) * mm});
            skArc(sketch, "E7.51.3", {"start": v(35.03, -5.75) * mm, "mid": v(35.4, -5.66) * mm, "end": v(35.6, -5.33) * mm});
            skLineSegment(sketch, "E7.51.4", {"start": v(35.03, -5.75) * mm, "end": v(34.53, -5.69) * mm});
            skLineSegment(sketch, "E7.51.5", {"start": v(34.9, -2.56) * mm, "end": v(35.92, -2.7) * mm, "construction": true});
            skLineSegment(sketch, "E7.52.0", {"start": v(35, -0.57) * mm, "end": v(35.5, -0.6) * mm});
            skArc(sketch, "E7.52.1", {"start": v(35.97, -1.11) * mm, "mid": v(35.84, -0.76) * mm, "end": v(35.5, -0.6) * mm});
            skLineSegment(sketch, "E7.52.2", {"start": v(35.97, -1.11) * mm, "end": v(35.93, -2.11) * mm});
            skArc(sketch, "E7.52.3", {"start": v(35.4, -2.6) * mm, "mid": v(35.76, -2.46) * mm, "end": v(35.93, -2.11) * mm});
            skLineSegment(sketch, "E7.52.4", {"start": v(35.4, -2.6) * mm, "end": v(34.9, -2.57) * mm});
            skLineSegment(sketch, "E7.52.5", {"start": v(35, 0.58) * mm, "end": v(36.02, 0.53) * mm, "construction": true});
            skLineSegment(sketch, "E7.53.0", {"start": v(34.9, 2.57) * mm, "end": v(35.4, 2.6) * mm});
            skArc(sketch, "E7.53.1", {"start": v(35.93, 2.11) * mm, "mid": v(35.76, 2.46) * mm, "end": v(35.4, 2.6) * mm});
            skLineSegment(sketch, "E7.53.2", {"start": v(35.93, 2.11) * mm, "end": v(35.97, 1.11) * mm});
            skArc(sketch, "E7.53.3", {"start": v(35.5, 0.6) * mm, "mid": v(35.84, 0.76) * mm, "end": v(35.97, 1.11) * mm});
            skLineSegment(sketch, "E7.53.4", {"start": v(35.5, 0.6) * mm, "end": v(35, 0.57) * mm});
            skLineSegment(sketch, "E7.53.5", {"start": v(34.8, 3.71) * mm, "end": v(35.83, 3.76) * mm, "construction": true});
            skLineSegment(sketch, "E7.54.0", {"start": v(34.53, 5.69) * mm, "end": v(35.03, 5.75) * mm});
            skArc(sketch, "E7.54.1", {"start": v(35.6, 5.33) * mm, "mid": v(35.4, 5.66) * mm, "end": v(35.03, 5.75) * mm});
            skLineSegment(sketch, "E7.54.2", {"start": v(35.6, 5.33) * mm, "end": v(35.73, 4.34) * mm});
            skArc(sketch, "E7.54.3", {"start": v(35.3, 3.77) * mm, "mid": v(35.63, 3.96) * mm, "end": v(35.73, 4.34) * mm});
            skLineSegment(sketch, "E7.54.4", {"start": v(35.3, 3.77) * mm, "end": v(34.8, 3.7) * mm});
            skLineSegment(sketch, "E7.54.5", {"start": v(34.33, 6.82) * mm, "end": v(35.35, 6.95) * mm, "construction": true});
            skLineSegment(sketch, "E7.55.0", {"start": v(33.89, 8.76) * mm, "end": v(34.37, 8.87) * mm});
            skArc(sketch, "E7.55.1", {"start": v(34.97, 8.5) * mm, "mid": v(34.75, 8.8) * mm, "end": v(34.37, 8.87) * mm});
            skLineSegment(sketch, "E7.55.2", {"start": v(34.97, 8.5) * mm, "end": v(35.2, 7.52) * mm});
            skArc(sketch, "E7.55.3", {"start": v(34.82, 6.92) * mm, "mid": v(35.13, 7.14) * mm, "end": v(35.2, 7.52) * mm});
            skLineSegment(sketch, "E7.55.4", {"start": v(34.82, 6.92) * mm, "end": v(34.33, 6.81) * mm});
            skLineSegment(sketch, "E7.55.5", {"start": v(33.58, 9.87) * mm, "end": v(34.58, 10.1) * mm, "construction": true});
            skLineSegment(sketch, "E7.56.0", {"start": v(32.96, 11.76) * mm, "end": v(33.44, 11.92) * mm});
            skArc(sketch, "E7.56.1", {"start": v(34.07, 11.6) * mm, "mid": v(33.82, 11.89) * mm, "end": v(33.44, 11.92) * mm});
            skLineSegment(sketch, "E7.56.2", {"start": v(34.07, 11.6) * mm, "end": v(34.38, 10.64) * mm});
            skArc(sketch, "E7.56.3", {"start": v(34.06, 10.01) * mm, "mid": v(34.35, 10.26) * mm, "end": v(34.38, 10.64) * mm});
            skLineSegment(sketch, "E7.56.4", {"start": v(34.06, 10.01) * mm, "end": v(33.58, 9.86) * mm});
            skLineSegment(sketch, "E7.56.5", {"start": v(32.56, 12.84) * mm, "end": v(33.54, 13.15) * mm, "construction": true});
            skLineSegment(sketch, "E7.57.0", {"start": v(31.78, 14.67) * mm, "end": v(32.24, 14.87) * mm});
            skArc(sketch, "E7.57.1", {"start": v(32.9, 14.6) * mm, "mid": v(32.62, 14.87) * mm, "end": v(32.24, 14.87) * mm});
            skLineSegment(sketch, "E7.57.2", {"start": v(32.9, 14.6) * mm, "end": v(33.29, 13.68) * mm});
            skArc(sketch, "E7.57.3", {"start": v(33.02, 13.03) * mm, "mid": v(33.3, 13.3) * mm, "end": v(33.29, 13.68) * mm});
            skLineSegment(sketch, "E7.57.4", {"start": v(33.02, 13.03) * mm, "end": v(32.56, 12.83) * mm});
            skLineSegment(sketch, "E7.57.5", {"start": v(31.28, 15.7) * mm, "end": v(32.22, 16.1) * mm, "construction": true});
            skLineSegment(sketch, "E7.58.0", {"start": v(30.33, 17.46) * mm, "end": v(30.77, 17.7) * mm});
            skArc(sketch, "E7.58.1", {"start": v(31.45, 17.5) * mm, "mid": v(31.16, 17.73) * mm, "end": v(30.77, 17.7) * mm});
            skLineSegment(sketch, "E7.58.2", {"start": v(31.45, 17.5) * mm, "end": v(31.93, 16.61) * mm});
            skArc(sketch, "E7.58.3", {"start": v(31.72, 15.93) * mm, "mid": v(31.96, 16.23) * mm, "end": v(31.93, 16.61) * mm});
            skLineSegment(sketch, "E7.58.4", {"start": v(31.72, 15.93) * mm, "end": v(31.28, 15.7) * mm});
            skLineSegment(sketch, "E7.58.5", {"start": v(29.75, 18.44) * mm, "end": v(30.65, 18.93) * mm, "construction": true});
            skLineSegment(sketch, "E7.59.0", {"start": v(28.65, 20.1) * mm, "end": v(29.06, 20.38) * mm});
            skArc(sketch, "E7.59.1", {"start": v(29.76, 20.24) * mm, "mid": v(29.44, 20.46) * mm, "end": v(29.06, 20.38) * mm});
            skLineSegment(sketch, "E7.59.2", {"start": v(29.76, 20.24) * mm, "end": v(30.3, 19.4) * mm});
            skArc(sketch, "E7.59.3", {"start": v(30.17, 18.71) * mm, "mid": v(30.38, 19.03) * mm, "end": v(30.3, 19.4) * mm});
            skLineSegment(sketch, "E7.59.4", {"start": v(30.17, 18.71) * mm, "end": v(29.75, 18.44) * mm});
            skLineSegment(sketch, "E7.59.5", {"start": v(27.97, 21.04) * mm, "end": v(28.83, 21.6) * mm, "construction": true});
            skLineSegment(sketch, "E7.60.0", {"start": v(26.73, 22.6) * mm, "end": v(27.12, 22.9) * mm});
            skArc(sketch, "E7.60.1", {"start": v(27.82, 22.83) * mm, "mid": v(27.49, 23.01) * mm, "end": v(27.12, 22.9) * mm});
            skLineSegment(sketch, "E7.60.2", {"start": v(27.82, 22.83) * mm, "end": v(28.45, 22.05) * mm});
            skArc(sketch, "E7.60.3", {"start": v(28.37, 21.34) * mm, "mid": v(28.55, 21.68) * mm, "end": v(28.45, 22.05) * mm});
            skLineSegment(sketch, "E7.60.4", {"start": v(28.37, 21.34) * mm, "end": v(27.98, 21.03) * mm});
            skLineSegment(sketch, "E7.60.5", {"start": v(25.97, 23.46) * mm, "end": v(26.78, 24.1) * mm, "construction": true});
            skLineSegment(sketch, "E7.61.0", {"start": v(24.6, 24.9) * mm, "end": v(24.96, 25.25) * mm});
            skArc(sketch, "E7.61.1", {"start": v(25.66, 25.23) * mm, "mid": v(25.31, 25.38) * mm, "end": v(24.96, 25.25) * mm});
            skLineSegment(sketch, "E7.61.2", {"start": v(25.66, 25.23) * mm, "end": v(26.36, 24.5) * mm});
            skArc(sketch, "E7.61.3", {"start": v(26.34, 23.8) * mm, "mid": v(26.5, 24.15) * mm, "end": v(26.36, 24.5) * mm});
            skLineSegment(sketch, "E7.61.4", {"start": v(26.34, 23.8) * mm, "end": v(25.98, 23.45) * mm});
            skLineSegment(sketch, "E7.61.5", {"start": v(23.77, 25.7) * mm, "end": v(24.5, 26.4) * mm, "construction": true});
            skLineSegment(sketch, "E7.62.0", {"start": v(22.27, 27) * mm, "end": v(22.6, 27.38) * mm});
            skArc(sketch, "E7.62.1", {"start": v(23.3, 27.43) * mm, "mid": v(22.94, 27.55) * mm, "end": v(22.6, 27.38) * mm});
            skLineSegment(sketch, "E7.62.2", {"start": v(23.3, 27.43) * mm, "end": v(24.05, 26.77) * mm});
            skArc(sketch, "E7.62.3", {"start": v(24.1, 26.07) * mm, "mid": v(24.22, 26.43) * mm, "end": v(24.05, 26.77) * mm});
            skLineSegment(sketch, "E7.62.4", {"start": v(24.1, 26.07) * mm, "end": v(23.77, 25.69) * mm});
            skLineSegment(sketch, "E7.62.5", {"start": v(21.37, 27.72) * mm, "end": v(22.04, 28.5) * mm, "construction": true});
            skLineSegment(sketch, "E7.63.0", {"start": v(19.76, 28.9) * mm, "end": v(20.05, 29.3) * mm});
            skArc(sketch, "E7.63.1", {"start": v(20.75, 29.4) * mm, "mid": v(20.38, 29.5) * mm, "end": v(20.05, 29.3) * mm});
            skLineSegment(sketch, "E7.63.2", {"start": v(20.75, 29.4) * mm, "end": v(21.56, 28.82) * mm});
            skArc(sketch, "E7.63.3", {"start": v(21.67, 28.12) * mm, "mid": v(21.76, 28.5) * mm, "end": v(21.56, 28.82) * mm});
            skLineSegment(sketch, "E7.63.4", {"start": v(21.67, 28.12) * mm, "end": v(21.37, 27.72) * mm});
            skLineSegment(sketch, "E7.63.5", {"start": v(18.8, 29.52) * mm, "end": v(19.4, 30.36) * mm, "construction": true});
            skLineSegment(sketch, "E7.64.0", {"start": v(17.09, 30.55) * mm, "end": v(17.34, 30.98) * mm});
            skArc(sketch, "E7.64.1", {"start": v(18.03, 31.15) * mm, "mid": v(17.65, 31.2) * mm, "end": v(17.34, 30.98) * mm});
            skLineSegment(sketch, "E7.64.2", {"start": v(18.03, 31.15) * mm, "end": v(18.89, 30.64) * mm});
            skArc(sketch, "E7.64.3", {"start": v(19.06, 29.95) * mm, "mid": v(19.11, 30.33) * mm, "end": v(18.89, 30.64) * mm});
            skLineSegment(sketch, "E7.64.4", {"start": v(19.06, 29.95) * mm, "end": v(18.8, 29.52) * mm});
            skLineSegment(sketch, "E7.64.5", {"start": v(16.08, 31.09) * mm, "end": v(16.6, 31.97) * mm, "construction": true});
            skLineSegment(sketch, "E7.65.0", {"start": v(14.28, 31.95) * mm, "end": v(14.5, 32.4) * mm});
            skArc(sketch, "E7.65.1", {"start": v(15.16, 32.64) * mm, "mid": v(14.78, 32.66) * mm, "end": v(14.5, 32.4) * mm});
            skLineSegment(sketch, "E7.65.2", {"start": v(15.16, 32.64) * mm, "end": v(16.06, 32.2) * mm});
            skArc(sketch, "E7.65.3", {"start": v(16.3, 31.54) * mm, "mid": v(16.32, 31.92) * mm, "end": v(16.06, 32.2) * mm});
            skLineSegment(sketch, "E7.65.4", {"start": v(16.3, 31.54) * mm, "end": v(16.08, 31.09) * mm});
            skLineSegment(sketch, "E7.65.5", {"start": v(13.22, 32.4) * mm, "end": v(13.67, 33.33) * mm, "construction": true});
            skLineSegment(sketch, "E7.66.0", {"start": v(11.36, 33.1) * mm, "end": v(11.53, 33.57) * mm});
            skArc(sketch, "E7.66.1", {"start": v(12.18, 33.87) * mm, "mid": v(11.8, 33.85) * mm, "end": v(11.53, 33.57) * mm});
            skLineSegment(sketch, "E7.66.2", {"start": v(12.18, 33.87) * mm, "end": v(13.11, 33.52) * mm});
            skArc(sketch, "E7.66.3", {"start": v(13.4, 32.87) * mm, "mid": v(13.4, 33.25) * mm, "end": v(13.11, 33.52) * mm});
            skLineSegment(sketch, "E7.66.4", {"start": v(13.4, 32.87) * mm, "end": v(13.23, 32.4) * mm});
            skLineSegment(sketch, "E7.66.5", {"start": v(10.27, 33.46) * mm, "end": v(10.63, 34.42) * mm, "construction": true});
            skLineSegment(sketch, "E7.67.0", {"start": v(8.34, 34) * mm, "end": v(8.48, 34.47) * mm});
            skArc(sketch, "E7.67.1", {"start": v(9.1, 34.82) * mm, "mid": v(8.71, 34.77) * mm, "end": v(8.48, 34.47) * mm});
            skLineSegment(sketch, "E7.67.2", {"start": v(9.1, 34.82) * mm, "end": v(10.06, 34.56) * mm});
            skArc(sketch, "E7.67.3", {"start": v(10.4, 33.94) * mm, "mid": v(10.36, 34.32) * mm, "end": v(10.06, 34.56) * mm});
            skLineSegment(sketch, "E7.67.4", {"start": v(10.4, 33.94) * mm, "end": v(10.27, 33.46) * mm});
            skLineSegment(sketch, "E7.67.5", {"start": v(7.23, 34.25) * mm, "end": v(7.5, 35.24) * mm, "construction": true});
            skLineSegment(sketch, "E7.68.0", {"start": v(5.26, 34.6) * mm, "end": v(5.35, 35.1) * mm});
            skArc(sketch, "E7.68.1", {"start": v(5.93, 35.5) * mm, "mid": v(5.56, 35.42) * mm, "end": v(5.35, 35.1) * mm});
            skLineSegment(sketch, "E7.68.2", {"start": v(5.93, 35.5) * mm, "end": v(6.92, 35.32) * mm});
            skArc(sketch, "E7.68.3", {"start": v(7.32, 34.74) * mm, "mid": v(7.24, 35.11) * mm, "end": v(6.92, 35.32) * mm});
            skLineSegment(sketch, "E7.68.4", {"start": v(7.32, 34.74) * mm, "end": v(7.23, 34.24) * mm});
            skLineSegment(sketch, "E7.68.5", {"start": v(4.13, 34.76) * mm, "end": v(4.3, 35.77) * mm, "construction": true});
            skLineSegment(sketch, "E7.69.0", {"start": v(2.14, 34.93) * mm, "end": v(2.18, 35.43) * mm});
            skArc(sketch, "E7.69.1", {"start": v(2.73, 35.89) * mm, "mid": v(2.36, 35.77) * mm, "end": v(2.18, 35.43) * mm});
            skLineSegment(sketch, "E7.69.2", {"start": v(2.73, 35.89) * mm, "end": v(3.72, 35.8) * mm});
            skArc(sketch, "E7.69.3", {"start": v(4.18, 35.25) * mm, "mid": v(4.06, 35.62) * mm, "end": v(3.72, 35.8) * mm});
            skLineSegment(sketch, "E7.69.4", {"start": v(4.18, 35.25) * mm, "end": v(4.13, 34.76) * mm});
            skLineSegment(sketch, "E7.69.5", {"start": v(1, 34.99) * mm, "end": v(1.09, 36) * mm, "construction": true});
            skArc(sketch, "E8.trimOffspring", {"start": v(2.14, 34.93) * mm, "mid": v(1.57, 34.96) * mm, "end": v(1, 34.99) * mm});
            skArc(sketch, "E9.trimOffspring", {"start": v(5.26, 34.6) * mm, "mid": v(4.7, 34.68) * mm, "end": v(4.13, 34.76) * mm});
            skArc(sketch, "E10.trimOffspring", {"start": v(8.34, 34) * mm, "mid": v(7.79, 34.12) * mm, "end": v(7.23, 34.25) * mm});
            skArc(sketch, "E11.trimOffspring", {"start": v(11.36, 33.1) * mm, "mid": v(10.81, 33.29) * mm, "end": v(10.27, 33.46) * mm});
            skArc(sketch, "E12.trimOffspring", {"start": v(14.28, 31.95) * mm, "mid": v(13.75, 32.18) * mm, "end": v(13.22, 32.4) * mm});
            skArc(sketch, "E13.trimOffspring", {"start": v(17.09, 30.55) * mm, "mid": v(16.58, 30.82) * mm, "end": v(16.08, 31.09) * mm});
            skArc(sketch, "E14.trimOffspring", {"start": v(19.76, 28.9) * mm, "mid": v(19.28, 29.21) * mm, "end": v(18.8, 29.52) * mm});
            skArc(sketch, "E15.trimOffspring", {"start": v(22.27, 27) * mm, "mid": v(21.82, 27.37) * mm, "end": v(21.37, 27.72) * mm});
            skArc(sketch, "E16.trimOffspring", {"start": v(24.6, 24.9) * mm, "mid": v(24.19, 25.3) * mm, "end": v(23.77, 25.7) * mm});
            skArc(sketch, "E17.trimOffspring", {"start": v(26.73, 22.6) * mm, "mid": v(26.36, 23.03) * mm, "end": v(25.97, 23.46) * mm});
            skArc(sketch, "E18.trimOffspring", {"start": v(28.65, 20.1) * mm, "mid": v(28.31, 20.57) * mm, "end": v(27.97, 21.04) * mm});
            skArc(sketch, "E19.trimOffspring", {"start": v(30.33, 17.46) * mm, "mid": v(30.04, 17.95) * mm, "end": v(29.75, 18.44) * mm});
            skArc(sketch, "E20.trimOffspring", {"start": v(31.78, 14.67) * mm, "mid": v(31.53, 15.19) * mm, "end": v(31.28, 15.7) * mm});
            skArc(sketch, "E21.trimOffspring", {"start": v(32.96, 11.76) * mm, "mid": v(32.77, 12.3) * mm, "end": v(32.56, 12.84) * mm});
            skArc(sketch, "E22.trimOffspring", {"start": v(33.89, 8.76) * mm, "mid": v(33.74, 9.31) * mm, "end": v(33.58, 9.87) * mm});
            skArc(sketch, "E23.trimOffspring", {"start": v(34.53, 5.69) * mm, "mid": v(34.44, 6.25) * mm, "end": v(34.33, 6.82) * mm});
            skArc(sketch, "E24.trimOffspring", {"start": v(34.9, 2.57) * mm, "mid": v(34.86, 3.14) * mm, "end": v(34.8, 3.71) * mm});
            skArc(sketch, "E25.trimOffspring", {"start": v(35, -0.57) * mm, "mid": v(35, 0) * mm, "end": v(35, 0.58) * mm});
            skArc(sketch, "E26.trimOffspring", {"start": v(34.8, -3.7) * mm, "mid": v(34.86, -3.13) * mm, "end": v(34.9, -2.56) * mm});
            skArc(sketch, "E27.trimOffspring", {"start": v(34.33, -6.81) * mm, "mid": v(34.44, -6.25) * mm, "end": v(34.54, -5.68) * mm});
            skArc(sketch, "E28.trimOffspring", {"start": v(33.58, -9.86) * mm, "mid": v(33.74, -9.3) * mm, "end": v(33.89, -8.75) * mm});
            skArc(sketch, "E29.trimOffspring", {"start": v(32.56, -12.83) * mm, "mid": v(32.77, -12.3) * mm, "end": v(32.97, -11.76) * mm});
            skArc(sketch, "E30.trimOffspring", {"start": v(31.28, -15.7) * mm, "mid": v(31.54, -15.18) * mm, "end": v(31.78, -14.66) * mm});
            skArc(sketch, "E31.trimOffspring", {"start": v(29.75, -18.44) * mm, "mid": v(30.05, -17.95) * mm, "end": v(30.34, -17.45) * mm});
            skArc(sketch, "E32.trimOffspring", {"start": v(27.98, -21.03) * mm, "mid": v(28.32, -20.57) * mm, "end": v(28.65, -20.1) * mm});
            skArc(sketch, "E33.trimOffspring", {"start": v(25.98, -23.45) * mm, "mid": v(26.36, -23.03) * mm, "end": v(26.73, -22.6) * mm});
            skArc(sketch, "E34.trimOffspring", {"start": v(23.77, -25.69) * mm, "mid": v(24.19, -25.3) * mm, "end": v(24.6, -24.9) * mm});
            skArc(sketch, "E35.trimOffspring", {"start": v(21.37, -27.72) * mm, "mid": v(21.82, -27.36) * mm, "end": v(22.27, -27) * mm});
            skArc(sketch, "E36.trimOffspring", {"start": v(18.8, -29.52) * mm, "mid": v(19.28, -29.2) * mm, "end": v(19.76, -28.89) * mm});
            skArc(sketch, "E37.trimOffspring", {"start": v(16.08, -31.09) * mm, "mid": v(16.59, -30.82) * mm, "end": v(17.1, -30.54) * mm});
            skArc(sketch, "E38.trimOffspring", {"start": v(13.23, -32.4) * mm, "mid": v(13.76, -32.18) * mm, "end": v(14.28, -31.95) * mm});
            skArc(sketch, "E39.trimOffspring", {"start": v(10.27, -33.46) * mm, "mid": v(10.82, -33.29) * mm, "end": v(11.36, -33.1) * mm});
            skArc(sketch, "E40.trimOffspring", {"start": v(7.23, -34.24) * mm, "mid": v(7.8, -34.12) * mm, "end": v(8.35, -33.99) * mm});
            skArc(sketch, "E41.trimOffspring", {"start": v(4.13, -34.76) * mm, "mid": v(4.7, -34.68) * mm, "end": v(5.27, -34.6) * mm});
            skArc(sketch, "E42.trimOffspring", {"start": v(1, -34.99) * mm, "mid": v(1.57, -34.96) * mm, "end": v(2.15, -34.93) * mm});
            skArc(sketch, "E43.trimOffspring", {"start": v(-2.14, -34.93) * mm, "mid": v(-1.57, -34.96) * mm, "end": v(-1, -34.99) * mm});
            skArc(sketch, "E44.trimOffspring", {"start": v(-5.26, -34.6) * mm, "mid": v(-4.7, -34.68) * mm, "end": v(-4.13, -34.76) * mm});
            skArc(sketch, "E45.trimOffspring", {"start": v(-8.34, -34) * mm, "mid": v(-7.79, -34.12) * mm, "end": v(-7.23, -34.25) * mm});
            skArc(sketch, "E46.trimOffspring", {"start": v(-11.36, -33.1) * mm, "mid": v(-10.81, -33.29) * mm, "end": v(-10.27, -33.46) * mm});
            skArc(sketch, "E47.trimOffspring", {"start": v(-14.28, -31.95) * mm, "mid": v(-13.75, -32.18) * mm, "end": v(-13.22, -32.4) * mm});
            skArc(sketch, "E48.trimOffspring", {"start": v(-17.09, -30.55) * mm, "mid": v(-16.58, -30.82) * mm, "end": v(-16.08, -31.09) * mm});
            skArc(sketch, "E49.trimOffspring", {"start": v(-19.76, -28.9) * mm, "mid": v(-19.28, -29.21) * mm, "end": v(-18.8, -29.52) * mm});
            skArc(sketch, "E50.trimOffspring", {"start": v(-22.27, -27) * mm, "mid": v(-21.82, -27.37) * mm, "end": v(-21.37, -27.72) * mm});
            skArc(sketch, "E51.trimOffspring", {"start": v(-24.6, -24.9) * mm, "mid": v(-24.19, -25.3) * mm, "end": v(-23.77, -25.7) * mm});
            skArc(sketch, "E52.trimOffspring", {"start": v(-26.73, -22.6) * mm, "mid": v(-26.36, -23.03) * mm, "end": v(-25.97, -23.46) * mm});
            skArc(sketch, "E53.trimOffspring", {"start": v(-28.65, -20.1) * mm, "mid": v(-28.31, -20.57) * mm, "end": v(-27.97, -21.04) * mm});
            skArc(sketch, "E54.trimOffspring", {"start": v(-30.33, -17.46) * mm, "mid": v(-30.04, -17.95) * mm, "end": v(-29.75, -18.44) * mm});
            skArc(sketch, "E55.trimOffspring", {"start": v(-31.78, -14.67) * mm, "mid": v(-31.53, -15.19) * mm, "end": v(-31.28, -15.7) * mm});
            skArc(sketch, "E56.trimOffspring", {"start": v(-32.96, -11.76) * mm, "mid": v(-32.77, -12.3) * mm, "end": v(-32.56, -12.84) * mm});
            skArc(sketch, "E57.trimOffspring", {"start": v(-35, 0.57) * mm, "mid": v(-35, 0) * mm, "end": v(-35, -0.58) * mm});
            skArc(sketch, "E58.trimOffspring", {"start": v(-34.8, 3.7) * mm, "mid": v(-34.86, 3.13) * mm, "end": v(-34.9, 2.56) * mm});
            skArc(sketch, "E59.trimOffspring", {"start": v(-34.33, 6.81) * mm, "mid": v(-34.44, 6.25) * mm, "end": v(-34.54, 5.68) * mm});
            skArc(sketch, "E60.trimOffspring", {"start": v(-33.58, 9.86) * mm, "mid": v(-33.74, 9.3) * mm, "end": v(-33.89, 8.75) * mm});
            skArc(sketch, "E61.trimOffspring", {"start": v(-32.56, 12.83) * mm, "mid": v(-32.77, 12.3) * mm, "end": v(-32.97, 11.76) * mm});
            skArc(sketch, "E62.trimOffspring", {"start": v(-33.89, -8.76) * mm, "mid": v(-33.74, -9.31) * mm, "end": v(-33.58, -9.87) * mm});
            skArc(sketch, "E63.trimOffspring", {"start": v(-34.53, -5.69) * mm, "mid": v(-34.44, -6.25) * mm, "end": v(-34.33, -6.82) * mm});
            skArc(sketch, "E64.trimOffspring", {"start": v(-34.9, -2.57) * mm, "mid": v(-34.86, -3.14) * mm, "end": v(-34.8, -3.71) * mm});
            skArc(sketch, "E65.trimOffspring", {"start": v(-31.28, 15.7) * mm, "mid": v(-31.54, 15.18) * mm, "end": v(-31.78, 14.66) * mm});
            skArc(sketch, "E66.trimOffspring", {"start": v(-29.75, 18.44) * mm, "mid": v(-30.05, 17.95) * mm, "end": v(-30.34, 17.45) * mm});
            skArc(sketch, "E67.trimOffspring", {"start": v(-27.98, 21.03) * mm, "mid": v(-28.32, 20.57) * mm, "end": v(-28.65, 20.1) * mm});
            skArc(sketch, "E68.trimOffspring", {"start": v(-25.98, 23.45) * mm, "mid": v(-26.36, 23.03) * mm, "end": v(-26.73, 22.6) * mm});
            skArc(sketch, "E69.trimOffspring", {"start": v(-23.77, 25.69) * mm, "mid": v(-24.19, 25.3) * mm, "end": v(-24.6, 24.9) * mm});
            skArc(sketch, "E70.trimOffspring", {"start": v(-21.37, 27.72) * mm, "mid": v(-21.82, 27.36) * mm, "end": v(-22.27, 27) * mm});
            skArc(sketch, "E71.trimOffspring", {"start": v(-18.8, 29.52) * mm, "mid": v(-19.28, 29.2) * mm, "end": v(-19.76, 28.89) * mm});
            skArc(sketch, "E72.trimOffspring", {"start": v(-16.08, 31.09) * mm, "mid": v(-16.59, 30.82) * mm, "end": v(-17.1, 30.54) * mm});
            skArc(sketch, "E73.trimOffspring", {"start": v(-4.13, 34.76) * mm, "mid": v(-4.7, 34.68) * mm, "end": v(-5.27, 34.6) * mm});
            skArc(sketch, "E74.trimOffspring", {"start": v(-13.23, 32.4) * mm, "mid": v(-13.76, 32.18) * mm, "end": v(-14.28, 31.95) * mm});
            skArc(sketch, "E75.trimOffspring", {"start": v(-10.27, 33.46) * mm, "mid": v(-10.82, 33.29) * mm, "end": v(-11.36, 33.1) * mm});
            skArc(sketch, "E76.trimOffspring", {"start": v(-7.23, 34.24) * mm, "mid": v(-7.8, 34.12) * mm, "end": v(-8.35, 33.99) * mm});
            skCircle(sketch, "E77", {"center": v(0, 0) * mm, "radius": 10 * mm});
            skSolve(sketch);
        }
        {
            var Q0;
            Q0 = qSketchRegion(id + "F0", true);
            extrude(context, id + "F1", {"entities" : qUnion([Q0]), "depth" : 6 * mm, "offsetDistance" : 25 * mm});
        }
    });
